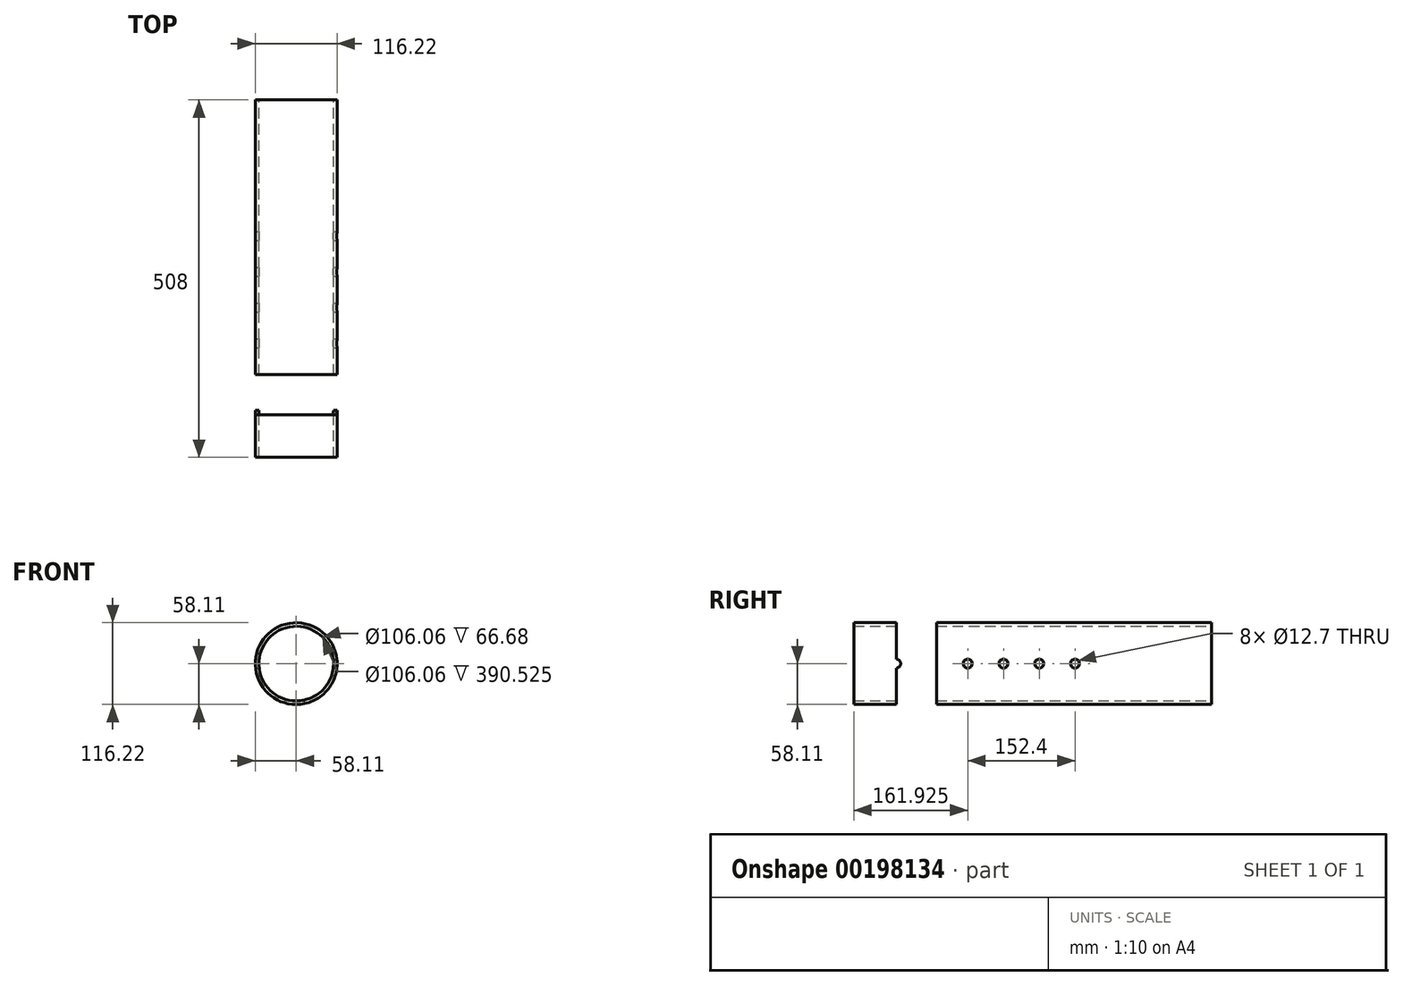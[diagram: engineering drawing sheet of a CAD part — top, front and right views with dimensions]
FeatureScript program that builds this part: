
annotation { "Feature Type Name" : "Feature", "Feature Type Description" : "" }
export const myFeature = defineFeature(function(context is Context, id is Id, definition is map)
    precondition{}
    {
        {
            var Q0;
            Q0=qCreatedBy(makeId("Front.planeOp"),FACE);
            var sketch = newSketch(context, id + "F0", { "sketchPlane" : qUnion([Q0])});
            skCircle(sketch, "E0", {"center": v(0, 0) * mm, "radius": 53.03 * mm});
            skCircle(sketch, "E1", {"center": v(0, 0) * mm, "radius": 58.11 * mm});
            skSolve(sketch);
        }
        {
            var Q0;
            Q0=makeQuery(id+"F0.imprint","IMPRINT",FACE,{"disambiguationData":[TD([[makeQuery(id+"F0.imprint","IMPRINT",EDGE,{"derivedFrom":sQuery(id+"F0.wireOp",EDGE,"E0")}),-1.0]])]});
            extrude(context, id + "F1", {"entities" : qUnion([Q0]), "endBound" : BoundingType.SYMMETRIC, "depth" : 508 * mm});
        }
        {
            var Q0;
            Q0=qCreatedBy(makeId("Right.planeOp"),FACE);
            var sketch = newSketch(context, id + "F2", { "sketchPlane" : qUnion([Q0])});
            skLineSegment(sketch, "E2.bottom", {"start": v(-193.68, 101.6) * mm, "end": v(193.67, 101.6) * mm});
            skLineSegment(sketch, "E2.top", {"start": v(-193.68, -101.6) * mm, "end": v(193.67, -101.6) * mm});
            skLineSegment(sketch, "E2.left", {"start": v(-193.68, 101.6) * mm, "end": v(-193.68, -101.6) * mm});
            skLineSegment(sketch, "E2.right", {"start": v(193.67, 101.6) * mm, "end": v(193.67, -101.6) * mm});
            skPoint(sketch, "E2.middle", {"position": v(0, 0) * mm});
            skLineSegment(sketch, "E3.bottom", {"start": v(193.67, 101.6) * mm, "end": v(-136.53, 101.6) * mm});
            skLineSegment(sketch, "E3.top", {"start": v(193.67, -101.6) * mm, "end": v(-136.53, -101.6) * mm});
            skLineSegment(sketch, "E3.left", {"start": v(193.67, 101.6) * mm, "end": v(193.68, -101.6) * mm});
            skLineSegment(sketch, "E3.right", {"start": v(-136.53, 101.6) * mm, "end": v(-136.53, -101.6) * mm});
            skLineSegment(sketch, "E4.bottom", {"start": v(193.67, 101.6) * mm, "end": v(-85.73, 101.6) * mm});
            skLineSegment(sketch, "E4.top", {"start": v(193.67, -101.6) * mm, "end": v(-85.73, -101.6) * mm});
            skLineSegment(sketch, "E4.right", {"start": v(-85.73, 101.6) * mm, "end": v(-85.73, -101.6) * mm});
            skLineSegment(sketch, "E5.bottom", {"start": v(193.67, 101.6) * mm, "end": v(-34.93, 101.6) * mm});
            skLineSegment(sketch, "E5.top", {"start": v(193.67, -101.6) * mm, "end": v(-34.93, -101.6) * mm});
            skLineSegment(sketch, "E5.right", {"start": v(-34.93, 101.6) * mm, "end": v(-34.93, -101.6) * mm});
            skLineSegment(sketch, "E6.bottom", {"start": v(193.67, 101.6) * mm, "end": v(3.17, 101.6) * mm});
            skLineSegment(sketch, "E6.top", {"start": v(193.67, -101.6) * mm, "end": v(0, -101.6) * mm});
            skLineSegment(sketch, "E7.bottom", {"start": v(193.67, 101.6) * mm, "end": v(15.88, 101.6) * mm});
            skLineSegment(sketch, "E7.top", {"start": v(193.67, -101.6) * mm, "end": v(15.88, -101.6) * mm});
            skLineSegment(sketch, "E7.right", {"start": v(15.87, 101.6) * mm, "end": v(15.88, -101.6) * mm});
            skLineSegment(sketch, "E8.bottom", {"start": v(193.67, 101.6) * mm, "end": v(66.67, 101.6) * mm});
            skLineSegment(sketch, "E8.top", {"start": v(193.67, -101.6) * mm, "end": v(66.67, -101.6) * mm});
            skLineSegment(sketch, "E8.right", {"start": v(66.67, 101.6) * mm, "end": v(66.68, -101.6) * mm});
            skCircle(sketch, "E9", {"center": v(-193.68, 0) * mm, "radius": 6.35 * mm});
            skCircle(sketch, "E10.1.0.0", {"center": v(-142.88, 0) * mm, "radius": 6.35 * mm});
            skCircle(sketch, "E10.2.0.0", {"center": v(-92.07, 0) * mm, "radius": 6.35 * mm});
            skCircle(sketch, "E10.3.0.0", {"center": v(-41.27, 0) * mm, "radius": 6.35 * mm});
            skCircle(sketch, "E10.4.0.0", {"center": v(9.53, 0) * mm, "radius": 6.35 * mm});
            skCircle(sketch, "E10.5.0.0", {"center": v(60.33, 0) * mm, "radius": 6.35 * mm});
            skLineSegment(sketch, "E10.direction1", {"start": v(-193.68, 0) * mm, "end": v(-142.88, 0) * mm, "construction": true});
            skSolve(sketch);
        }
        {
            var Q0;
            Q0=makeQuery(id+"F2.imprint","IMPRINT",FACE,{"disambiguationData":[TD([[makeQuery(id+"F2.imprint","IMPRINT",EDGE,{"derivedFrom":sQuery(id+"F2.wireOp",EDGE,"E10.1.0.0")}),1.0]])]});
            var Q1;
            Q1=makeQuery(id+"F2.imprint","IMPRINT",FACE,{"disambiguationData":[TD([[makeQuery(id+"F2.imprint","IMPRINT",EDGE,{"derivedFrom":sQuery(id+"F2.wireOp",EDGE,"E10.3.0.0")}),1.0]])]});
            var Q2;
            Q2=makeQuery(id+"F2.imprint","IMPRINT",FACE,{"disambiguationData":[TD([[makeQuery(id+"F2.imprint","IMPRINT",EDGE,{"derivedFrom":sQuery(id+"F2.wireOp",EDGE,"E10.2.0.0")}),1.0]])]});
            var Q3;
            Q3=makeQuery(id+"F2.imprint","IMPRINT",FACE,{"disambiguationData":[TD([[makeQuery(id+"F2.imprint","IMPRINT",EDGE,{"derivedFrom":sQuery(id+"F2.wireOp",EDGE,"E10.4.0.0")}),1.0]])]});
            var Q4;
            Q4=makeQuery(id+"F2.imprint","IMPRINT",FACE,{"disambiguationData":[TD([[makeQuery(id+"F2.imprint","IMPRINT",EDGE,{"derivedFrom":sQuery(id+"F2.wireOp",EDGE,"E10.5.0.0")}),1.0]])]});
            var Q5;
            {var subQ0=sQuery(id+"F2.wireOp",EDGE,"E9");var subQ1=sQuery(id+"F2.wireOp",EDGE,"E2.left");var subQ2=makeQuery(id+"F2.imprint","INTERSECT",VERTEX,{"disambiguationData":[OD(0.0)],"derivedFrom":[subQ1,subQ0]});Q5=makeQuery(id+"F2.imprint","IMPRINT",FACE,{"disambiguationData":[TD([[makeQuery(id+"F2.imprint","IMPRINT",EDGE,{"disambiguationData":[TD([[subQ2,-1.0]])],"derivedFrom":subQ1}),-1.0]])]});}
            var Q6;
            {var subQ0=sQuery(id+"F2.wireOp",EDGE,"E9");var subQ1=sQuery(id+"F2.wireOp",EDGE,"E2.left");var subQ2=makeQuery(id+"F2.imprint","INTERSECT",VERTEX,{"disambiguationData":[OD(0.0)],"derivedFrom":[subQ1,subQ0]});Q6=makeQuery(id+"F2.imprint","IMPRINT",FACE,{"disambiguationData":[TD([[makeQuery(id+"F2.imprint","IMPRINT",EDGE,{"disambiguationData":[TD([[subQ2,-1.0]])],"derivedFrom":subQ1}),1.0]])]});}
            extrude(context, id + "F3", {"entities" : qUnion([Q0, Q1, Q2, Q3, Q4, Q5, Q6]), "operationType" : NewBodyOperationType.REMOVE, "endBound" : BoundingType.SYMMETRIC, "oppositeDirection" : true, "depth" : 762 * mm});
        }
    });
